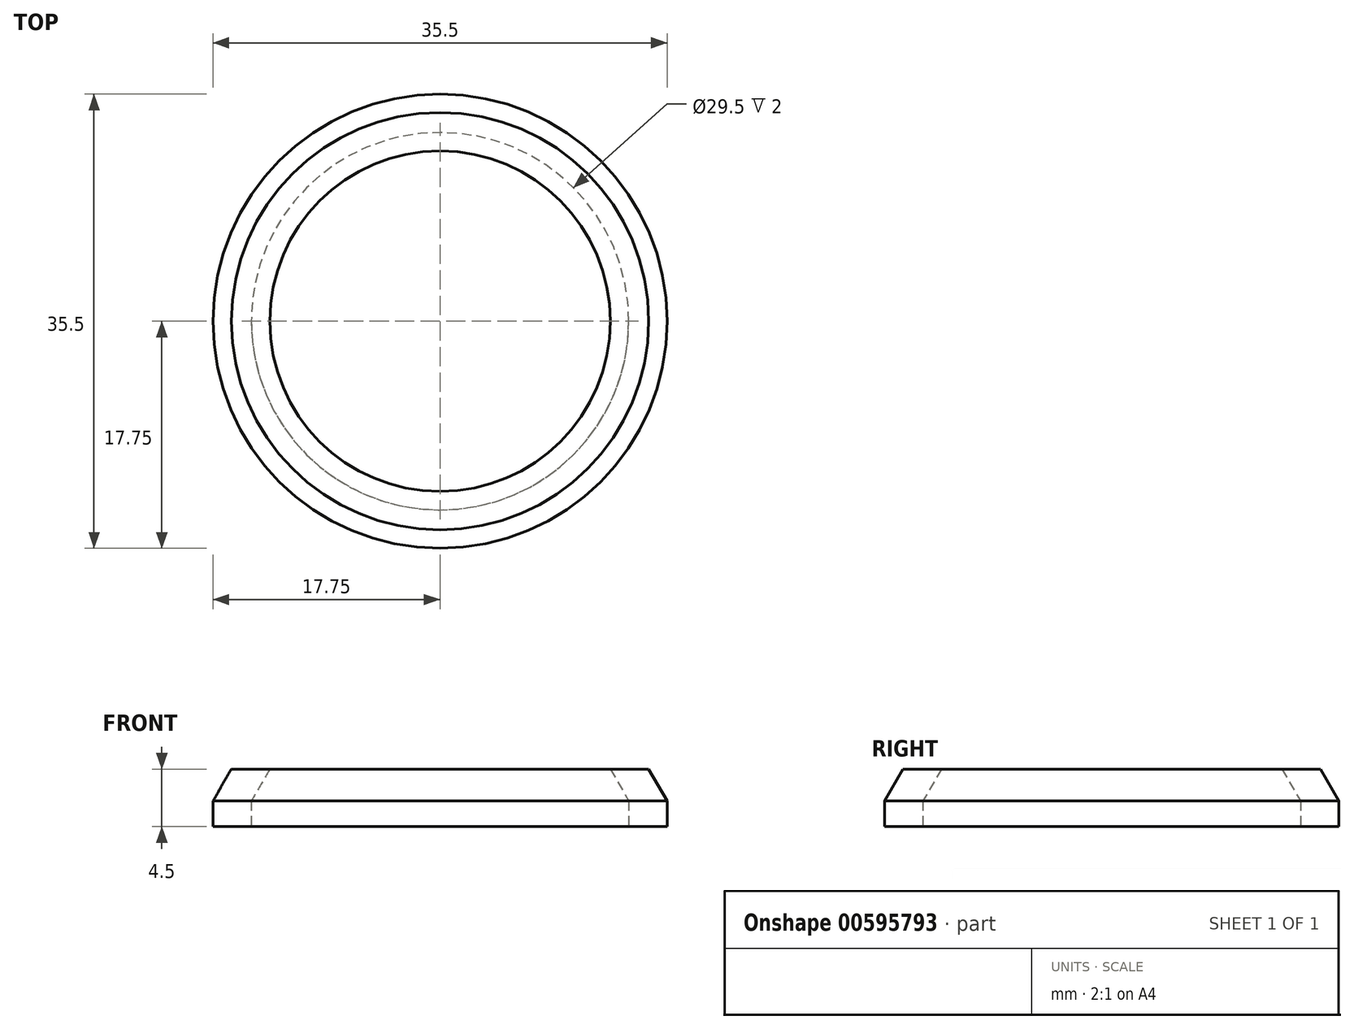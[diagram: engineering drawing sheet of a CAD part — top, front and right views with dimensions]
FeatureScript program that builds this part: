
annotation { "Feature Type Name" : "Feature", "Feature Type Description" : "" }
export const myFeature = defineFeature(function(context is Context, id is Id, definition is map)
    precondition{}
    {
        {
            var Q0;
            Q0=qCreatedBy(makeId("Top.planeOp"),FACE);
            var sketch = newSketch(context, id + "F0", { "sketchPlane" : qUnion([Q0])});
            skCircle(sketch, "E0", {"center": v(0, 0) * mm, "radius": 14.75 * mm});
            skCircle(sketch, "E1", {"center": v(0, 0) * mm, "radius": 17.75 * mm});
            skSolve(sketch);
        }
        {
            var Q0;
            Q0 = qSketchRegion(id + "F0", true);
            extrude(context, id + "F1", {"entities" : qUnion([Q0]), "depth" : 2 * mm, "offsetDistance" : 25.4 * mm});
        }
        {
            var Q0;
            Q0=qCreatedBy(makeId("Front.planeOp"),FACE);
            var sketch = newSketch(context, id + "F2", { "sketchPlane" : qUnion([Q0])});
            skLineSegment(sketch, "E2.0", {"start": v(-17.75, 2) * mm, "end": v(17.75, 2) * mm});
            skLineSegment(sketch, "E3", {"start": v(-17.75, 2) * mm, "end": v(-16.3, 4.5) * mm});
            skLineSegment(sketch, "E4", {"start": v(-16.3, 4.5) * mm, "end": v(-13.3, 4.5) * mm});
            skLineSegment(sketch, "E5", {"start": v(-13.3, 4.5) * mm, "end": v(-14.75, 2) * mm});
            skLineSegment(sketch, "E6", {"start": v(0, 2) * mm, "end": v(0, 4.78) * mm, "construction": true});
            skPoint(sketch, "E6.endSnap0", {"position": v(0, 2) * mm});
            skSolve(sketch);
        }
        {
            var Q0;
            Q0 = qSketchRegion(id + "F2", true);
            var Q1;
            Q1=sQuery(id+"F2.wireOp",EDGE,"E6");
            revolve(context, id + "F3", {"operationType" : NewBodyOperationType.ADD, "entities" : qUnion([Q0]), "axis" : qUnion([Q1]), "revolveType" : RevolveType.FULL});
        }
    });
